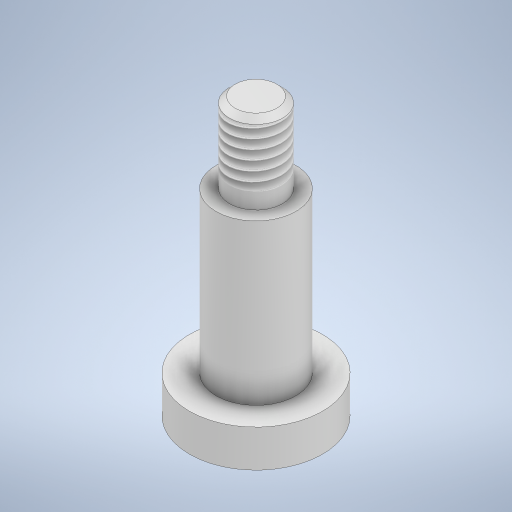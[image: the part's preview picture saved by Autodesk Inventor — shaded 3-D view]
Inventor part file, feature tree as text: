
AUTODESK INVENTOR PART (.ipt)
format: ipt  version: 2024.2 (Build 282272000, 272)  size: 288,768 bytes
history: native  units: mm
features: sketch x2, revolve x1, thread x1, extrude x1, chamfer x1
ambient origin geometry x8: Origin, YZ Plane, XZ Plane, XY Plane, X Axis, Y Axis, Z Axis, Center Point
bodies: Solid1 (feature_tree)
feature tree (6):
  revolve  "Revolution1"  [1 undecoded]
  thread  "Thread1"  [1 undecoded]
  extrude  "Extrusion1"  Depth=12.0mm
  chamfer  "Chamfer1"  Distance=2.8mm
  sketch  "Sketch1"  dims[d0=10.0mm d1=6.0mm d2=4.0mm]
  sketch  "Sketch2"  dims[d3=6.0mm d4=12.0mm d5=2.8mm d6=90.0deg d7=6.0mm d8=1.2mm d9=2.5mm d10=2.0mm d11=0.0mm d12=0.43mm d13=2.0mm d14=45.0deg]
note: 2 required parameter values undecoded (feature->parameter linkage not recoverable at this tier; creation-order binding heuristic only, values carry confidence <= 0.55)